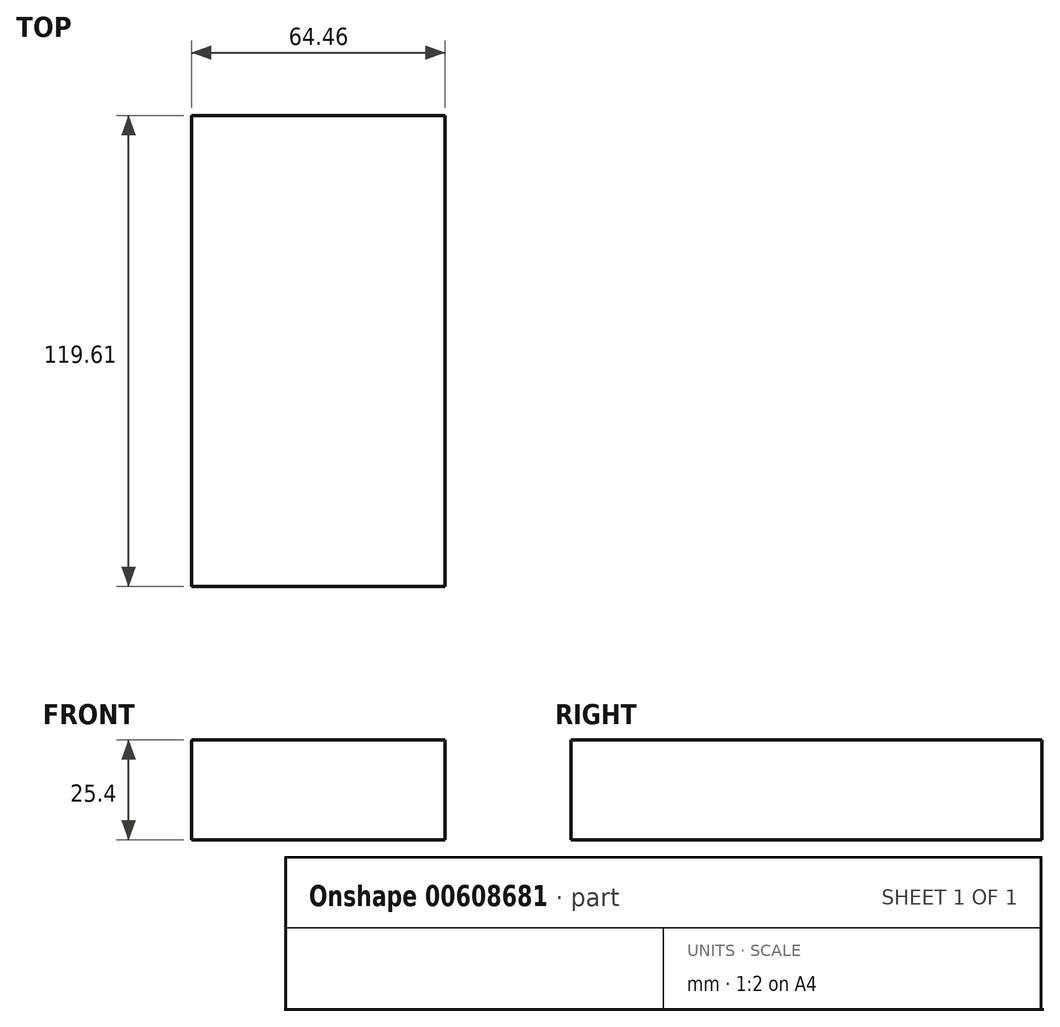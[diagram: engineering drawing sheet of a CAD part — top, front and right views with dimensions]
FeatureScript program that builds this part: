
annotation { "Feature Type Name" : "Feature", "Feature Type Description" : "" }
export const myFeature = defineFeature(function(context is Context, id is Id, definition is map)
    precondition{}
    {
        {
            var Q0;
            Q0=qCreatedBy(makeId("Top.planeOp"),FACE);
            var sketch = newSketch(context, id + "F0", { "sketchPlane" : qUnion([Q0])});
            skLineSegment(sketch, "E0.bottom", {"start": v(0, 51.53) * mm, "end": v(64.46, 51.53) * mm});
            skLineSegment(sketch, "E0.top", {"start": v(0, -68.08) * mm, "end": v(64.46, -68.08) * mm});
            skLineSegment(sketch, "E0.left", {"start": v(0, 51.53) * mm, "end": v(0, -68.08) * mm});
            skLineSegment(sketch, "E0.right", {"start": v(64.46, 51.53) * mm, "end": v(64.46, -68.08) * mm});
            skSolve(sketch);
        }
        {
            var Q0;
            Q0 = qSketchRegion(id + "F0", true);
            extrude(context, id + "F1", {"entities" : qUnion([Q0]), "depth" : 25.4 * mm, "offsetDistance" : 25.4 * mm});
        }
    });
